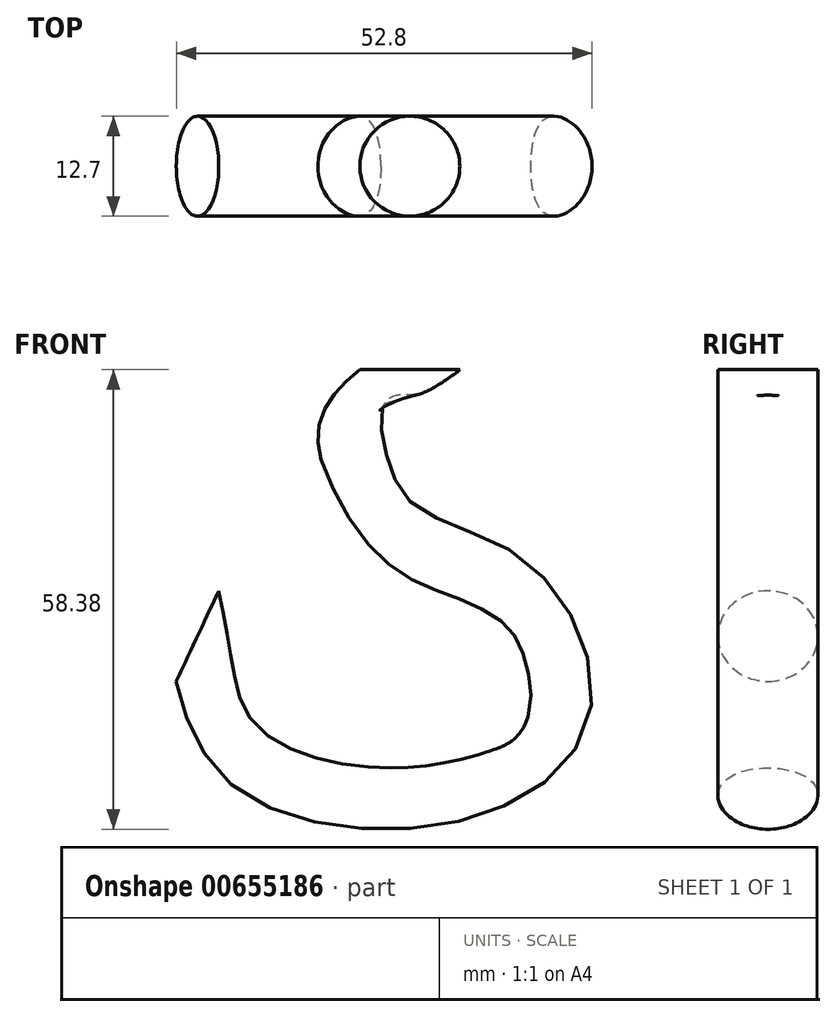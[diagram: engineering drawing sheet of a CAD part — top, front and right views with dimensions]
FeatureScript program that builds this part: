
annotation { "Feature Type Name" : "Feature", "Feature Type Description" : "" }
export const myFeature = defineFeature(function(context is Context, id is Id, definition is map)
    precondition{}
    {
        {
            var Q0;
            Q0=qCreatedBy(makeId("Front.planeOp"),FACE);
            var sketch = newSketch(context, id + "F0", { "sketchPlane" : qUnion([Q0])});
            skFitSpline(sketch, "E0", {"points": [v(-27.35, 0) * mm, v(-32.95, -5.34) * mm, v(-33.7, -10.43) * mm, v(-27.6, -20.86) * mm, v(-14.12, -29) * mm, v(-9.54, -44.01) * mm, v(-24.55, -53.68) * mm, v(-47.2, -49.1) * mm, v(-54.32, -33.84) * mm], "startDerivative": vector(-70.96, -56.14) * mm, "endDerivative": vector(-29.3, 124.87) * mm});
            skSolve(sketch);
        }
        {
            var Q0;
            Q0=qCreatedBy(makeId("Top.planeOp"),FACE);
            var sketch = newSketch(context, id + "F1", { "sketchPlane" : qUnion([Q0])});
            skPoint(sketch, "E1.0", {"position": v(-27.35, 0) * mm});
            skCircle(sketch, "E2", {"center": v(-27.35, 0) * mm, "radius": 6.35 * mm});
            skSolve(sketch);
        }
        {
            var Q0;
            Q0=makeQuery(id+"F1.imprint","IMPRINT",FACE,{"disambiguationData":[TD([[makeQuery(id+"F1.imprint","IMPRINT",EDGE,{"derivedFrom":sQuery(id+"F1.wireOp",EDGE,"E2")}),1.0]])]});
            var Q1;
            Q1=sQuery(id+"F0.wireOp",EDGE,"E0");
            sweep(context, id + "F2", {"profiles" : qUnion([Q0]), "path" : qUnion([Q1])});
        }
    });
